# Revit family: for update_28912XXX_new
name_source: partatom
category: Furniture
revit_build: Autodesk Revit 2018 (Build: 20170223_1515(x64)
units: mm (PartAtom-declared; Revit-internal decimal feet)

## family parameters
Cut with Voids When Loaded = Yes
Host = Face
OmniClass Number = 23.31.25.00
OmniClass Title = Toilet and Bath Specialties
Room Calculation Point = No
Shared = No

## types (1)
- 210 Sand Recycled
    Always visible = Yes
    BIMobject category = Bathroom Accessories
    Default Elevation = 1219 mm
    Description = WallStoris Planet Edition Storage basket
    Design country = Germany
    EAN code = 4059625479414
    Edition number = 1
    IFC Classification = Furnishing Element
    Manufacturer = Hansgrohe
    Manufacturer country = Germany
    Manufacturer name = hansgrohe
    Masterformat 2014 Code = 10 28 00
    Masterformat 2014 Description = Toilet, Bath, and Laundry Accessories
    Material = Hansgrohe - Plastic - 210 Sand Recycled
    Model = 28912XXX
    OmniClass Code = 23-31 25 00
    OmniClass Description = Toilet and Bath Specialties
    Product Guid = 0d19b06c-8bc0-4f31-94b0-404421e1c739
    Product SKU = 28912XXX
    Product data url = https://bimobject.com
    Product family = Cosmetic boxes
    Product group = WallStoris Planet Edition
    Product name = WallStoris Planet Edition Storage basket
    Product url = https://pro.hansgrohe.com
    QR code = https://bimobject.com
    UNSPSC Code = 301815
    URL = https://www.hansgrohe.com
    Uniclass 2015 Code = Pr_40_20_87_76
    Uniclass 2015 Name = Shower heads
    Uniformat II Code = E2010
    Uniformat II Description = Fixed Furnishings
    Version = 1
    Weight Net (Kg) = 150

## geometry (parser evidence)
native form markers: Sweep x1
no freeform markers — native parametric forms only
